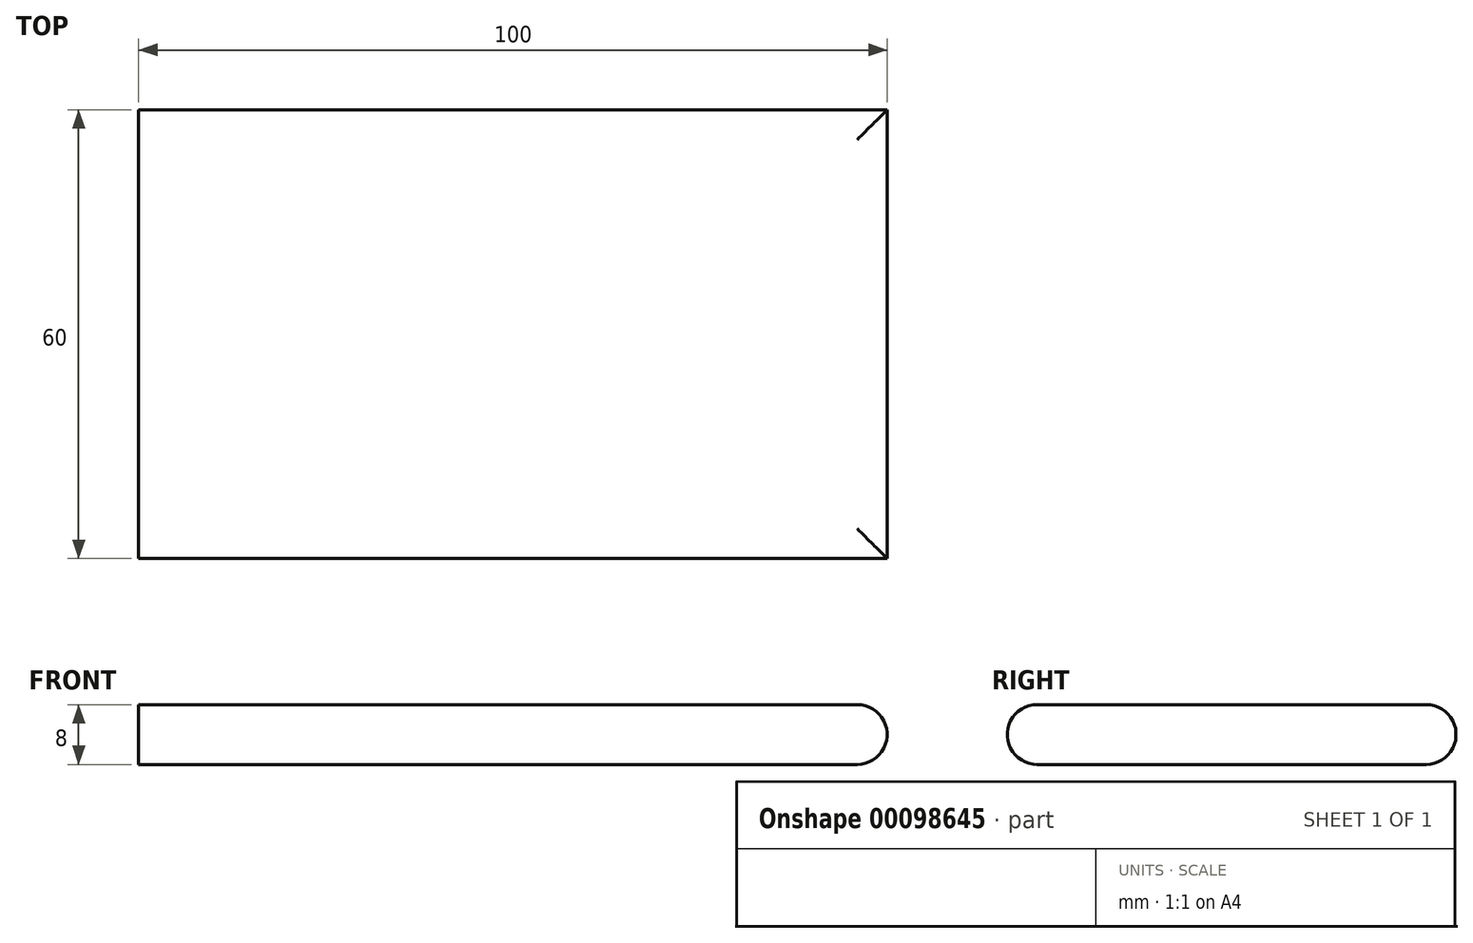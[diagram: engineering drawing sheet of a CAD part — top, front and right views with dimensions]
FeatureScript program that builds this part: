
annotation { "Feature Type Name" : "Feature", "Feature Type Description" : "" }
export const myFeature = defineFeature(function(context is Context, id is Id, definition is map)
    precondition{}
    {
        {
            var Q0;
            Q0=qCreatedBy(makeId("Top.planeOp"),FACE);
            var sketch = newSketch(context, id + "F0", { "sketchPlane" : qUnion([Q0])});
            skLineSegment(sketch, "E0.bottom", {"start": v(50, 30) * mm, "end": v(-50, 30) * mm});
            skLineSegment(sketch, "E0.top", {"start": v(50, -30) * mm, "end": v(-50, -30) * mm});
            skLineSegment(sketch, "E0.left", {"start": v(50, 30) * mm, "end": v(50, -30) * mm});
            skLineSegment(sketch, "E0.right", {"start": v(-50, 30) * mm, "end": v(-50, -30) * mm});
            skPoint(sketch, "E0.middle", {"position": v(0, 0) * mm});
            skSolve(sketch);
        }
        {
            var Q0;
            Q0=makeQuery(id+"F0.imprint","IMPRINT",FACE,{"disambiguationData":[TD([[makeQuery(id+"F0.imprint","IMPRINT",EDGE,{"derivedFrom":sQuery(id+"F0.wireOp",EDGE,"E0.bottom")}),1.0]])]});
            extrude(context, id + "F1", {"entities" : qUnion([Q0]), "depth" : 8 * mm});
        }
        {
            var Q0;
            Q0=makeQuery(id+"F1.opExtrude","CAP_EDGE",EDGE,{"disambiguationData":[OSD([sQuery(id+"F0.wireOp",EDGE,"E0.top")])],"isStart":false});
            var Q1;
            Q1=makeQuery(id+"F1.opExtrude","CAP_EDGE",EDGE,{"disambiguationData":[OSD([sQuery(id+"F0.wireOp",EDGE,"E0.top")])],"isStart":true});
            var Q2;
            Q2=makeQuery(id+"F1.opExtrude","CAP_EDGE",EDGE,{"disambiguationData":[OSD([sQuery(id+"F0.wireOp",EDGE,"E0.left")])],"isStart":false});
            var Q3;
            Q3=makeQuery(id+"F1.opExtrude","CAP_EDGE",EDGE,{"disambiguationData":[OSD([sQuery(id+"F0.wireOp",EDGE,"E0.left")])],"isStart":true});
            var Q4;
            Q4=makeQuery(id+"F1.opExtrude","CAP_EDGE",EDGE,{"disambiguationData":[OSD([sQuery(id+"F0.wireOp",EDGE,"E0.bottom")])],"isStart":false});
            var Q5;
            Q5=makeQuery(id+"F1.opExtrude","CAP_EDGE",EDGE,{"disambiguationData":[OSD([sQuery(id+"F0.wireOp",EDGE,"E0.bottom")])],"isStart":true});
            fillet(context, id + "F2", {"entities" : qUnion([Q0, Q1, Q2, Q3, Q4, Q5]), "radius" : 4 * mm, "tangentPropagation" : true, "allowEdgeOverflow" : false});
        }
    });
